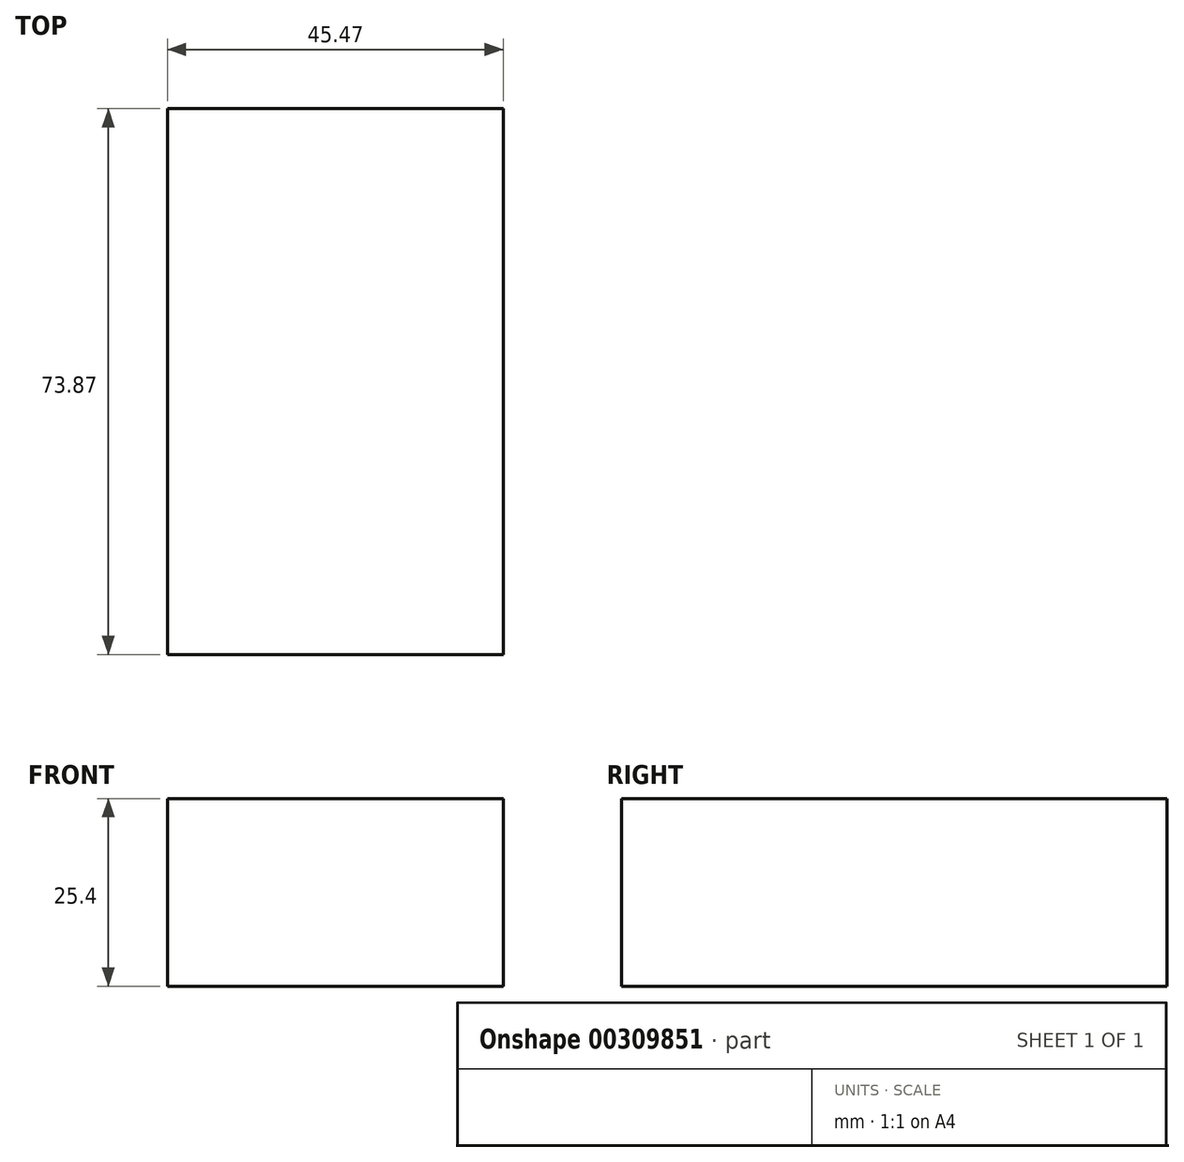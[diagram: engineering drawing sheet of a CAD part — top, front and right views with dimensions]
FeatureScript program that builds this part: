
annotation { "Feature Type Name" : "Feature", "Feature Type Description" : "" }
export const myFeature = defineFeature(function(context is Context, id is Id, definition is map)
    precondition{}
    {
        {
            var Q0;
            Q0=qCreatedBy(makeId("Top.planeOp"),FACE);
            var sketch = newSketch(context, id + "F0", { "sketchPlane" : qUnion([Q0])});
            skLineSegment(sketch, "E0.bottom", {"start": v(0, 25.53) * mm, "end": v(45.47, 25.53) * mm});
            skLineSegment(sketch, "E0.top", {"start": v(0, 0) * mm, "end": v(45.47, 0) * mm});
            skLineSegment(sketch, "E0.left", {"start": v(0, 25.53) * mm, "end": v(0, 0) * mm});
            skLineSegment(sketch, "E0.right", {"start": v(45.47, 25.53) * mm, "end": v(45.47, 0) * mm});
            skLineSegment(sketch, "E1.bottom", {"start": v(0, 73.87) * mm, "end": v(45.47, 73.87) * mm});
            skLineSegment(sketch, "E1.left", {"start": v(0, 73.87) * mm, "end": v(0, 25.53) * mm});
            skLineSegment(sketch, "E1.right", {"start": v(45.47, 73.87) * mm, "end": v(45.47, 25.53) * mm});
            skSolve(sketch);
        }
        {
            var Q0;
            Q0 = qSketchRegion(id + "F0", true);
            extrude(context, id + "F1", {"entities" : qUnion([Q0]), "depth" : 25.4 * mm});
        }
    });
